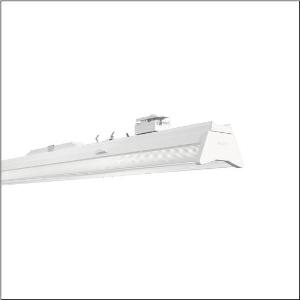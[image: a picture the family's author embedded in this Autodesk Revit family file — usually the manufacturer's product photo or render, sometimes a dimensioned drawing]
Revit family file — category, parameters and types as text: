
# Revit family: licross_r__21_performance_mo_52td16cn66xg_bcc0
name_source: partatom
category: Lighting Fixtures
units: mm (PartAtom-declared; Revit-internal decimal feet)

## family parameters
Cut with Voids When Loaded = No
Host = Face
Light Source = No
Part Type = Normal
Room Calculation Point = No
Round Connector Dimension = Use Diameter
Shared = No

## types (1)
- --- (1 x LED, 5970 lm, 32.8 W, 6500K)
    Apparent Load = 33 VA
    CIE Flux Codes = 66 88 96 79 100
    Color Rendering = 80
    Color Temperature = 6500K
    Default Elevation = 1800 mm
    Description = Licross® 21 Performance MO, luminaire insert, of sheet steel, galvanised, coil coated, white, length: 1.500mm, width: 120mm, height: 123mm, LED rated luminous flux: 5.970lm, light colour: 865, SDCM (Standard Deviation of Colour Matching)MacAdam ≤ 3 SDCM (initial), control gear: ON/OFF Multilumen, CLOi, with plug, 3-pole, with phase selection, mains connection: 220..240V, AC, 50/60Hz, start of lifetime: 33W, end of service life: 39W, internal wiring halogen-free, primary light control with lens, of plastic, primary optical cover: cover, of PMMA, light emission: direct/indirect distribution, primary light characteristic: symmetric, protection rating (complete): IP54, insulation class (complete): insulation class I (protective earthing), certification: CE, ENEC, UKCA, protection symbol: D if used in an environment with non-conductive dust loads with corresponding accessories, impact resistance: IK06, permissible ambient temperature for indoor applications: -35..+55°C, corresponds to IFS (International Featured Standards) requirements for safety and quality in the food industry, reducing of maximum allowable ambient temperature of 5°C with ceiling mounting, LABS conformity tested according to VDMA 24364:2018-05, packaging unit: 1 piece
    Height = 114 mm
    Lamp = 1 x LED
    Lamp Light Flux = 5970 lm
    Lamp Power = 32.8 W
    Lamp count = 1
    Length = 1500 mm
    Luminous efficacy = 182 lm/W
    Manufacturer = Siteco
    ModVariant = No
    Model = 52TD16CN66XG
    Mounting Place = Ceiling
    Mounting Type = Pendant
    Number of Poles = 1
    OnlyDefault = Yes
    Power Factor = 1
    Product Name = Licross® 21 Performance MO
    Product group = luminaire insert | ceiling pendant
    ProductGroupID = 901
    Protection Class = Protection class I
    Protection Degree = IP 54
    RLX_Detail_Level = 1
    RLX_Emergency_Light_Flux = 0 lm
    RLX_Emergency_Type = 0
    RLX_Emergency_Type_DB = No
    RlxData = <blob elided: 31853 chars, md5=b74448a1>
    Socket = socket
    Standby Power = 0 W
    System Light Flux = 5970 lm
    System Power = 33 W
    Type Comments = factory setting: luminous flux: 100 % | (A | C | E) | 76 mA
    Type Image = l_1256138.jpg
    URL = http://relux.com
    VarID = @adj_058727
    Voltage = 0 V
    Weight = 0.00 kg
    Width = 120 mm

## geometry (parser evidence)
native form markers: Blend x4, Sweep x13
no freeform markers — native parametric forms only
